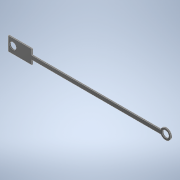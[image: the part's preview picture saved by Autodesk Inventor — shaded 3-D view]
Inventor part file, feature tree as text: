
AUTODESK INVENTOR PART (.ipt)
format: ipt  version: 2022 (Build 260153000, 153)  size: 116,224 bytes
history: native  units: in
note: dims shown in document units (in); Inventor stores cm internally (conversion verified against a paired STEP export)
features: other x1, extrude x1, sketch x1
ambient origin geometry x8: Origin, YZ Plane, XZ Plane, XY Plane, X Axis, Y Axis, Z Axis, Center Point
bodies: Body1 (feature_tree)
feature tree (3):
  other  "Sólido1"
  extrude  "Extrusión1"  Depth=0.0157in
  sketch  "Boceto1"  dims[d6=0.0984in d8=0.0984in d9=0.1575in d10=2.2835in d11=0.0591in d12=0.0157in d13=0.0in]
